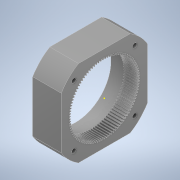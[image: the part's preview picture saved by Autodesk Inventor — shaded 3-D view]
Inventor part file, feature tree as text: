
AUTODESK INVENTOR PART (.ipt)
format: ipt  version: 2022 (Build 260153000, 153)  size: 659,456 bytes
history: mixed  units: in
note: dims shown in document units (in); Inventor stores cm internally (conversion verified against a paired STEP export)
features: sketch x5, extrude x4, other x1, imported_body x1
ambient origin geometry x8: Origin, YZ Plane, XZ Plane, XY Plane, X Axis, Y Axis, Z Axis, Center Point
bodies: Solid1 (imported_parasolid)
feature tree (11):
  extrude  "Extrusion1"  Depth=0.3937in TaperAngle=0.0deg
  extrude  "Extrusion2"  Depth=0.3937in
  extrude  "Extrusion3"  Depth=0.1181in
  sketch  "Sketch5"  dims[d10=0.0in d11=0.0in]
  extrude  "Extrusion4"  [1 undecoded]
  sketch  "Sketch2"  dims[d1=0.2756in d2=0.0in d3=0.3937in d4=0.0in]
  sketch  "Sketch3"  dims[d5=0.3937in d6=0.0in d7=0.1181in]
  sketch  "Sketch4"  dims[d8=0.1181in d9=0.1181in]
  sketch  "Sketch6"
  other  "96_Teeth_Gear.STEP"
  imported_body  NMx_Import_Brep_tag  [imported B-rep: ~399 faces, bbox_mm=[20.0, 60.0, 60.0]]
note: 1 required parameter value undecoded (feature->parameter linkage not recoverable at this tier; creation-order binding heuristic only, values carry confidence <= 0.55)
